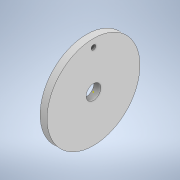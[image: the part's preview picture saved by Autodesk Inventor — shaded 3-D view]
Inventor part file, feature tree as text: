
AUTODESK INVENTOR PART (.ipt)
format: ipt  version: 2020 (Build 240168000, 168)  size: 104,448 bytes
history: native  units: mm
features: sketch x3, extrude x2
ambient origin geometry x8: Origin, YZ Plane, XZ Plane, XY Plane, X Axis, Y Axis, Z Axis, Center Point
bodies: Solid1 (feature_tree)
feature tree (5):
  extrude  "Extrusion1"  Depth=6.35mm
  sketch  "Sketch2"  dims[d2=3.0mm d3=0.0mm d4=2.0mm]
  extrude  "Extrusion2"  Depth=2.0mm
  sketch  "Sketch1"  dims[d0=40.0mm d1=6.35mm]
  sketch  "Sketch3"  dims[d5=2.0mm d6=0.0mm]
